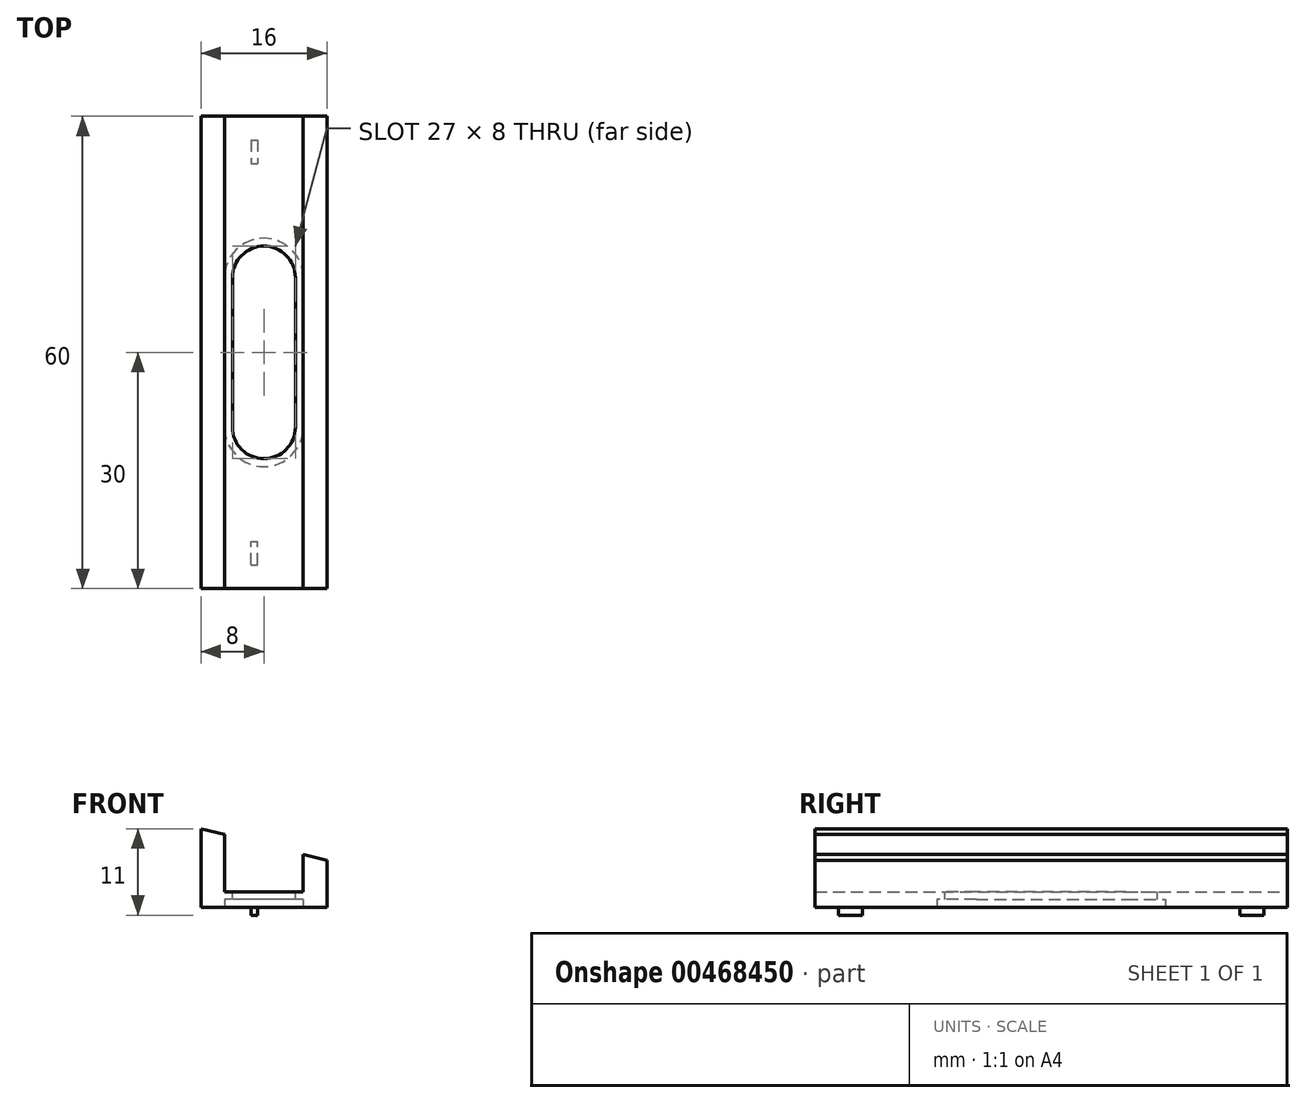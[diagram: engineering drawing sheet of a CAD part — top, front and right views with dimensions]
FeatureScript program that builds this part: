
annotation { "Feature Type Name" : "Feature", "Feature Type Description" : "" }
export const myFeature = defineFeature(function(context is Context, id is Id, definition is map)
    precondition{}
    {
        {
            var Q0;
            Q0=qCreatedBy(makeId("Front.planeOp"),FACE);
            var sketch = newSketch(context, id + "F0", { "sketchPlane" : qUnion([Q0])});
            skLineSegment(sketch, "E0", {"start": v(0, 0) * mm, "end": v(16, 0) * mm});
            skLineSegment(sketch, "E1", {"start": v(16, 0) * mm, "end": v(16, 6) * mm});
            skLineSegment(sketch, "E2", {"start": v(16, 6) * mm, "end": v(13, 6.75) * mm});
            skLineSegment(sketch, "E3", {"start": v(0, 10) * mm, "end": v(0, 0) * mm});
            skLineSegment(sketch, "E4", {"start": v(3, 9.25) * mm, "end": v(3, 2) * mm});
            skLineSegment(sketch, "E5", {"start": v(3, 2) * mm, "end": v(13, 2) * mm});
            skLineSegment(sketch, "E6", {"start": v(13, 2) * mm, "end": v(13, 6.75) * mm});
            skLineSegment(sketch, "E7", {"start": v(8, -112.85) * mm, "end": v(8, -112.85) * mm});
            skPoint(sketch, "E7.startSnap0", {"position": v(8, 17.26) * mm});
            skPoint(sketch, "E8", {"position": v(8, 2) * mm});
            skPoint(sketch, "E9.orphan", {"position": v(13, 17.43) * mm});
            skPoint(sketch, "E10.orphan", {"position": v(3, 17.1) * mm});
            skLineSegment(sketch, "E11.trimOffspring", {"start": v(3, 9.25) * mm, "end": v(0, 10) * mm});
            skSolve(sketch);
        }
        {
            var Q0;
            Q0 = qSketchRegion(id + "F0", true);
            var Q1;
            Q1 = qSketchRegion(id + "F2", true);
            extrude(context, id + "F1", {"entities" : qUnion([Q0, Q1]), "depth" : 60 * mm});
        }
        {
            var Q0;
            Q0=makeQuery(id+"F1.opExtrude","SWEPT_FACE",FACE,{"disambiguationData":[OSD([sQuery(id+"F0.wireOp",EDGE,"E5")])]});
            var sketch = newSketch(context, id + "F2", { "sketchPlane" : qUnion([Q0])});
            skLineSegment(sketch, "E12", {"start": v(-23.34, -30) * mm, "end": v(35.45, -30) * mm, "construction": true});
            skLineSegment(sketch, "E13.left", {"start": v(4, -20.5) * mm, "end": v(4, -39.5) * mm});
            skLineSegment(sketch, "E13.right", {"start": v(12, -20.5) * mm, "end": v(12, -39.5) * mm});
            skArc(sketch, "E14", {"start": v(12, -20.5) * mm, "mid": v(8, -16.5) * mm, "end": v(4, -20.5) * mm});
            skArc(sketch, "E15", {"start": v(4, -39.5) * mm, "mid": v(8, -43.5) * mm, "end": v(12, -39.5) * mm});
            skSolve(sketch);
        }
        {
            var Q0;
            Q0 = qSketchRegion(id + "F2", true);
            extrude(context, id + "F3", {"entities" : qUnion([Q0]), "operationType" : NewBodyOperationType.REMOVE, "endBound" : BoundingType.THROUGH_ALL, "oppositeDirection" : true, "depth" : 25 * mm});
        }
        {
            var Q0;
            Q0=qCreatedBy(makeId("Top.planeOp"),FACE);
            var sketch = newSketch(context, id + "F4", { "sketchPlane" : qUnion([Q0])});
            skLineSegment(sketch, "E16.left", {"start": v(3, -20.5) * mm, "end": v(3, -39.5) * mm});
            skLineSegment(sketch, "E16.right", {"start": v(13, -20.5) * mm, "end": v(13, -39.5) * mm});
            skArc(sketch, "E17", {"start": v(13, -20.5) * mm, "mid": v(8, -15.5) * mm, "end": v(3, -20.5) * mm});
            skArc(sketch, "E18", {"start": v(3, -39.5) * mm, "mid": v(8, -44.5) * mm, "end": v(13, -39.5) * mm});
            skSolve(sketch);
        }
        {
            var Q0;
            Q0 = qSketchRegion(id + "F4", true);
            extrude(context, id + "F5", {"entities" : qUnion([Q0]), "operationType" : NewBodyOperationType.REMOVE, "depth" : 1 * mm});
        }
        {
            var Q0;
            Q0=qCreatedBy(makeId("Top.planeOp"),FACE);
            var sketch = newSketch(context, id + "F6", { "sketchPlane" : qUnion([Q0])});
            skLineSegment(sketch, "E19.bottom", {"start": v(6.4, -3) * mm, "end": v(7.2, -3) * mm});
            skLineSegment(sketch, "E19.top", {"start": v(6.4, -6) * mm, "end": v(7.2, -6) * mm});
            skLineSegment(sketch, "E19.left", {"start": v(6.4, -3) * mm, "end": v(6.4, -6) * mm});
            skLineSegment(sketch, "E19.right", {"start": v(7.2, -3) * mm, "end": v(7.2, -6) * mm});
            skLineSegment(sketch, "E20", {"start": v(0, -30) * mm, "end": v(17.98, -30) * mm, "construction": true});
            skLineSegment(sketch, "E21.MirrorCS", {"start": v(6.4, -57) * mm, "end": v(6.4, -54) * mm});
            skLineSegment(sketch, "E22.MirrorCS", {"start": v(6.4, -57) * mm, "end": v(7.2, -57) * mm});
            skLineSegment(sketch, "E23.MirrorCS", {"start": v(7.2, -57) * mm, "end": v(7.2, -54) * mm});
            skLineSegment(sketch, "E24.MirrorCS", {"start": v(6.4, -54) * mm, "end": v(7.2, -54) * mm});
            skSolve(sketch);
        }
        {
            var Q0;
            Q0 = qSketchRegion(id + "F6", true);
            extrude(context, id + "F7", {"entities" : qUnion([Q0]), "operationType" : NewBodyOperationType.ADD, "oppositeDirection" : true, "depth" : 1 * mm});
        }
    });
